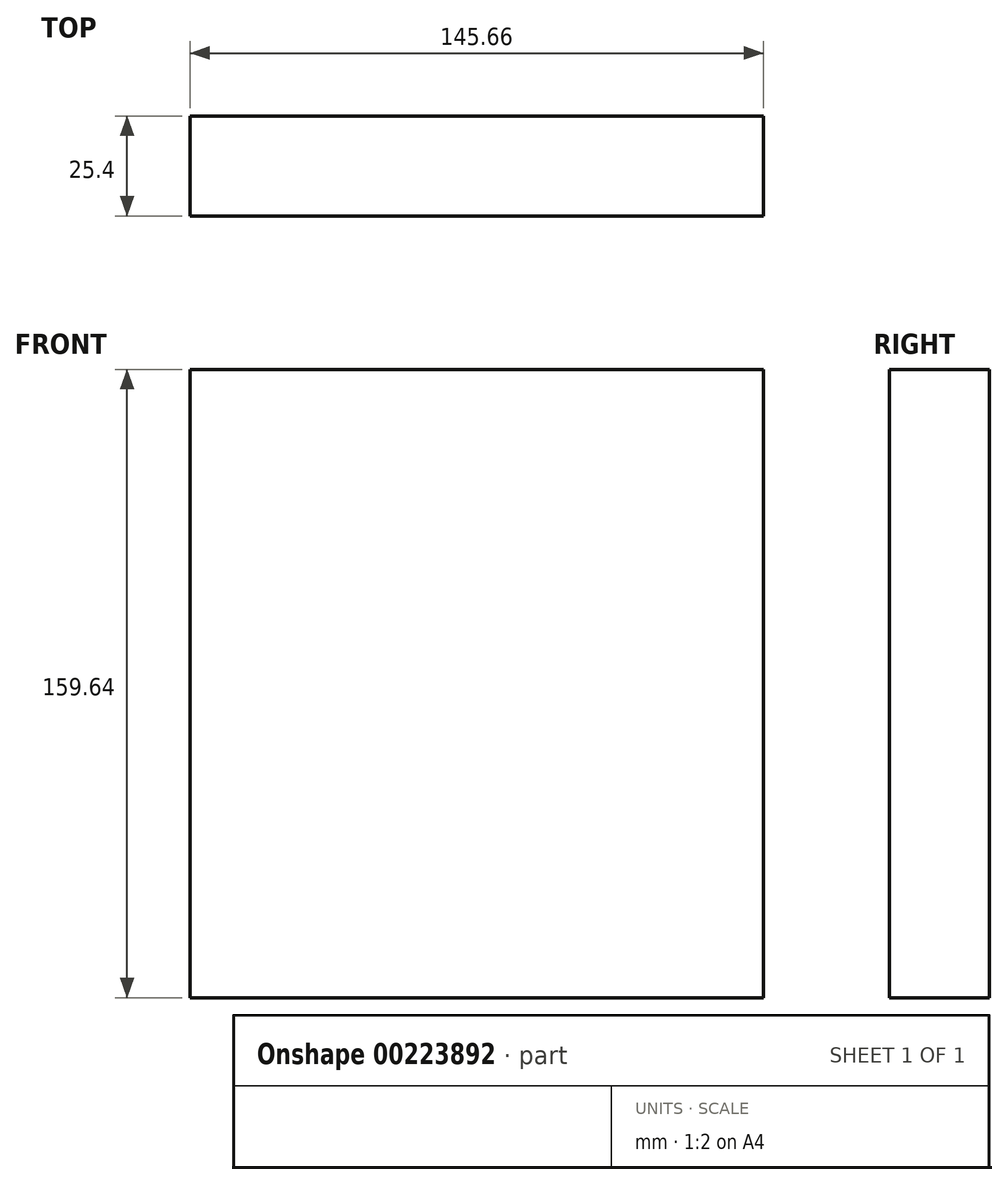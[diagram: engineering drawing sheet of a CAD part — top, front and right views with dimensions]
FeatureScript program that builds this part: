
annotation { "Feature Type Name" : "Feature", "Feature Type Description" : "" }
export const myFeature = defineFeature(function(context is Context, id is Id, definition is map)
    precondition{}
    {
        {
            var Q0;
            Q0=qCreatedBy(makeId("Front.planeOp"),FACE);
            var sketch = newSketch(context, id + "F0", { "sketchPlane" : qUnion([Q0])});
            skLineSegment(sketch, "E0.bottom", {"start": v(-70.62, 78.93) * mm, "end": v(75.04, 78.93) * mm});
            skLineSegment(sketch, "E0.top", {"start": v(-70.62, -80.7) * mm, "end": v(75.04, -80.7) * mm});
            skLineSegment(sketch, "E0.left", {"start": v(-70.62, 78.93) * mm, "end": v(-70.62, -80.7) * mm});
            skLineSegment(sketch, "E0.right", {"start": v(75.04, 78.93) * mm, "end": v(75.04, -80.7) * mm});
            skSolve(sketch);
        }
        {
            var Q0;
            Q0 = qSketchRegion(id + "F0", true);
            extrude(context, id + "F1", {"entities" : qUnion([Q0]), "depth" : 25.4 * mm});
        }
    });
